# Revit family: Camera-Security-Panasonic-Super_Dynamic-Dome-AI-H265-Network-X2251LSeriesX
name_source: partatom
category: Security Devices
units: mm (PartAtom-declared; Revit-internal decimal feet)

## family parameters
Cut with Voids When Loaded = No
Host = Face
Maintain Annotation Orientation = No
OmniClass Number = 23.85.10.14.11
OmniClass Title = Cameras
Part Type = Normal
Room Calculation Point = No
Round Connector Dimension = Use Diameter
Shared = No

## types (2) — shared parameters
4K = Resolution : 4K
5M = Resolution : 5M
Alarm Input Or Output Specification = ALARM IN 1(Alarm input 1/ Black & white input/ Auto time adjustment input) (x1), ALARM IN 2 (Alarm input 2/ ALARM OUT) (x1) , ALARM IN 3 (Alarm input 3/ AUX OUT) (x1)
Audio In = Yes
Audio Out = Yes
Base Bracket Height = 1.417 "
Base Height = 2.244 "
Base Radius = 2.549 "
Communication Ports = 10Base-T / 100Base-TX, RJ45 connector
Day Or Night = Yes
Decoration Cover Height = 0.618 "
Decoration Cover Hole Radius = 1.634 "
Decoration Cover Radius = 3.661 "
Decoration Cover Wall Height = 0.118 "
Diameter = 5.098 "
Dome Bottom Offset = 0.197 "
Dome Diameter = 3.268 "
Equipment Abbreviation = SC
Family Version = 1.0.0
Full HD = Resolution : Full HD
HD = Resolution : HD
Has Base Bracket = No
Has POE = Yes
Height = 4.075 "
IP Or Analog = IP
Indoor Or Outdoor = Indoor
Manufacturer = Panasonic
Model Disclaimer = Contact Panasonic for more information
Mounting Positions = Surface Mount
Operational Humidity = 10 to 90 % (no condensation)
Operational Temperature = 14 °F to 122 °F
Pan Max = 180.00°
Pan Min = -180.00°
Panning Range = -180 to +180
Power Active = 10.7 W
Product Documentation Link = https://bizpartner.panasonic.net
Product Material = Paint - Panasonic -i-Pro White
Product Page URL = https://security.panasonic.com
Provide Feedback = https://www.surveymonkey.com
Regulatory Compliance = UL (UL60950-1), c-UL (CSA C22.2 No.60950-1), CE, IEC60950-1, FCC (Part15 ClassA), ICES003 ClassA, EN55032 ClassB, EN55024
Shock Resistance = IK10 (IEC 62262)
Storage Temperature = 14 °F to 122 °F
Tilt Max = 85.00°
Tilt Min = -30.00°
Tilting Range = -30 to +85
URL = http://security.panasonic.com
Vandal Resistant = Yes
Voltage DC = 12 V
WQHD = Resolution : WQHD
Wide Dynamic Range = Yes
Yaw Max = 100.00°
Yaw Min = -100.00°
Yawing Range = -100 to +100
z Camera Radius = 2.549 "
z Camera Radius2 = 1.784 "
z Const Pan Handle Length = 19.488 "
z Const Tilt Base Length = 9.843 "
z Const Tilt Base2 Length = 19.685 "
z Const Tilt Handle Length = 11.811 "
z Const Yaw Base Length = 10.236 "
z Const Yaw Base2 Length = 17.323 "
z Const Yaw Handle Length = 9.252 "
z Dome Radius = 1.634 "
z Embedded Bottom Offset = -1.673 "
z Level Offset = 7.874 "
zero-valued in all types: Default Elevation, z Zero

## per-type parameters (varying)
| type | Angle Of View | Camera Number | Date Last Modified | Description | HFOV Max 169 | HFOV Max 43 | HFOV Min 169 | HFOV Min 43 | Minimum Illumination | Part Description | VFOV Max 169 | VFOV Max 43 | VFOV Min 169 | VFOV Min 43 | z VV Viewpoint Depth Max | z VV Viewpoint Depth Min |
| WV-X2251L | 105 | 2251 | 2020/05/12 | Security Camera, Fixed Dome, Network, Super Dynamic , AI, H.264, 5M, WV-X2251L | 105.00° | 105.00° | 33.00° | 33.00° | 0.070 lx | Security Camera, Fixed Dome, Network, Super Dynamic , AI, H.264, 5M, WV-X2251L | 56.00° | 56.00° | 19.00° | 19.00° | 1.185 " | 1.185 " |
| WV-X2271L | 101 | 2271 | 2020/08/25 | Security Camera, Fixed Dome, Network, Super Dynamic , AI, H.264, 4K, WV-X2271L | 101.00° | 101.00° | 52.00° | 52.00° | 0.090 lx | Security Camera, Fixed Dome, Network, Super Dynamic , AI, H.264, 4K, WV-X2271L | 55.00° | 55.00° | 29.00° | 29.00° | 1.28 " | 1.28 " |

note: column(s) folded — value = type name in every type: Model, Part Number

## geometry (parser evidence)
native form markers: Blend x2, Sweep x11
no freeform markers — native parametric forms only
